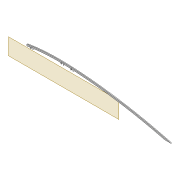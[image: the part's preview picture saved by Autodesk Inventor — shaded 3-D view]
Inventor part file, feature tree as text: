
AUTODESK INVENTOR PART (.ipt)
format: ipt  version: 2022 (Build 260153000, 153)  size: 508,928 bytes
history: native  units: mm
features: extrude x8, sketch x7, projected_geometry x7, fillet x2, shell x1, plane x1, chamfer x1
ambient origin geometry x8: Origin, YZ Plane, XZ Plane, XY Plane, X Axis, Y Axis, Z Axis, Center Point
bodies: Solid1 (feature_tree)
feature tree (27):
  extrude  "Extrusion1"  Depth=4.0mm
  shell  "Shell1"  Thickness=2.0mm
  extrude  "Extrusion8"  Depth=5.9mm
  extrude  "Extrusion3"  Depth=10.0mm TaperAngle=0.0deg
  extrude  "Extrusion4"  Depth=5.0mm
  fillet  "Fillet1"  Radius=5.0mm
  sketch  "Sketch10"  dims[d22=2.0mm d23=0.0mm d31=2.0mm d32=5.0mm]
  extrude  "Extrusion5"  Depth=2.5mm
  plane  "Work Plane2"
  extrude  "Extrusion9"  Depth=5.0mm
  fillet  "Fillet2"  Radius=2.5mm
  extrude  "Extrusion10"  Depth=5.0mm
  chamfer  "Chamfer1"  Distance=2.0mm
  extrude  "Extrusion12"  Depth=20.0mm
  sketch  "Sketch3"  dims[d0=2.0mm d1=0.0mm d2=4.0mm d7=2.0mm]
  sketch  "Sketch8"  dims[d8=2.0mm d9=5.9mm]
  sketch  "Sketch9"  dims[d13=10.0mm d14=0.0mm d16=10.0mm d17=0.0mm]
  projected_geometry  "Projected Loop4"
  projected_geometry  "Projected Loop10"
  sketch  "Sketch24"  dims[d34=1.6mm d35=2.5mm]
  projected_geometry  "Projected Loop11"
  projected_geometry  "Projected Loop12"
  projected_geometry  "Projected Loop13"
  sketch  "Sketch26"  dims[d37=5.0mm d38=1.6mm d40=2.5mm]
  projected_geometry  "Projected Loop14"
  sketch  "Sketch29"  dims[d62=80.0mm d63=5.0mm d64=2.0mm d65=0.0mm d66=2.5mm d67=12.0mm d68=5.0mm d69=15.0mm d70=12.0mm d71=3.05mm d72=10.0mm d73=0.0mm d74=2.0mm d75=90.0mm d76=20.0mm d77=0.5mm d78=10.0mm d79=0.0mm d82=10.0mm d83=3.0mm d84=2.0mm d85=45.0deg d86=0.0mm d87=1.0mm d88=1.0mm d89=1.0mm d90=1.0mm d91=1.0mm d92=10.0mm d93=0.0mm]
  projected_geometry  "Project Cut Edges1"
